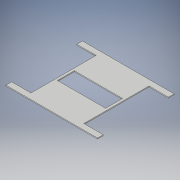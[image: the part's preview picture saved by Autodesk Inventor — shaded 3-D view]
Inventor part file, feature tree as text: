
AUTODESK INVENTOR PART (.ipt)
format: ipt  version: 2019 (Build 230136000, 136)  size: 131,584 bytes
history: native  units: mm
features: extrude x3, sketch x3, other x1
ambient origin geometry x8: Origin, YZ Plane, XZ Plane, XY Plane, X Axis, Y Axis, Z Axis, Center Point
bodies: Body1 (feature_tree)
feature tree (7):
  other  "Bryła1"
  extrude  "Wyciągnięcie proste1"  Depth=81.0mm
  extrude  "Wyciągnięcie proste2"  Depth=56.0mm
  extrude  "Wyciągnięcie proste4"  Depth=28.0mm
  sketch  "Szkic1"
  sketch  "Szkic2"
  sketch  "Szkic3"
